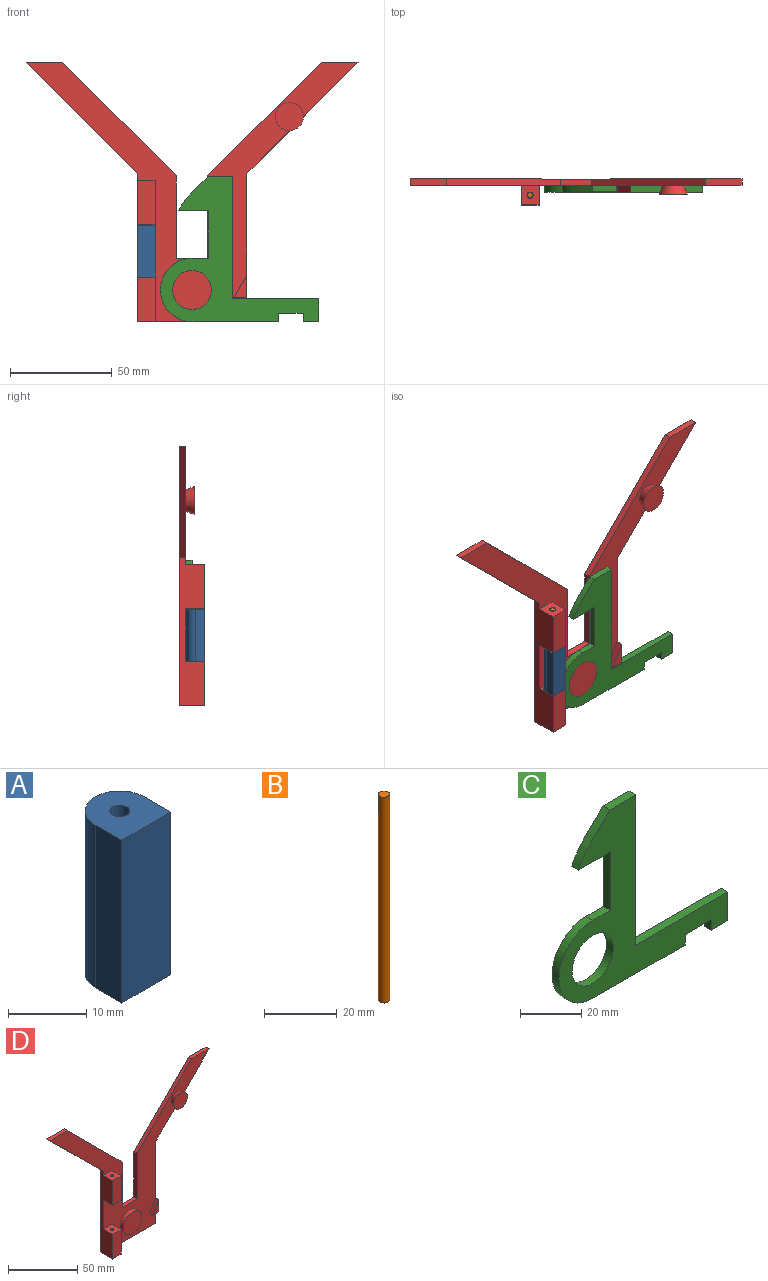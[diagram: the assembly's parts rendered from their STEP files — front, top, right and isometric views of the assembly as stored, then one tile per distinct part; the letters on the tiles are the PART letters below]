
ASSEMBLY  parts=4 mates=3
PART A: 7 faces, bbox 8.8x9.2x25.4 mm
  f0: cylinder r=4.41mm len=25.4mm, axis (0,0,-1), area 352mm2, adj f1,f4,f5,f6
  f1: plane 25.4x4.76mm, normal (-1,0,0), area 121mm2, adj f0,f2,f5,f6
  f2: plane 25.4x8.82mm, normal (0,-1,0), area 224.1mm2, adj f1,f4,f5,f6
  f3: cylinder r=1.27mm len=25.4mm, axis (0,0,-1), area 202.7mm2, adj f5,f6
  f4: plane 25.4x4.76mm, normal (1,0,0), area 121mm2, adj f0,f2,f5,f6
  f5: plane 9.17x8.82mm, normal (0,0,1), area 67.5mm2, adj f0,f1,f2,f3,f4
  f6: plane 9.17x8.82mm, normal (0,0,-1), area 67.5mm2, adj f0,f1,f2,f3,f4
PART B: 3 faces, bbox 3x3x69.3 mm
  f0: cylinder r=1.52mm len=69.34mm, axis (0,0,1), area 664mm2, adj f1,f2
  f1: plane 3.05x3.05mm, normal (0,0,-1), area 7.3mm2, adj f0
  f2: plane 3.05x3.05mm, normal (0,0,1), area 7.3mm2, adj f0
PART C: 17 faces, bbox 77.8x3.2x71.3 mm
  f0: plane 8.14x3.18mm, normal (0,0,1), area 25.8mm2, adj f1,f13,f15,f16
  f1: cylinder r=15.54mm len=31.08mm, axis (0,1,0), area 155mm2, adj f0,f2,f15,f16
  f2: plane 42.57x3.18mm, normal (0,0,-1), area 135.2mm2, adj f1,f3,f15,f16
  f3: plane 4.14x3.18mm, normal (1,0,0), area 13.2mm2, adj f2,f4,f15,f16
  f4: plane 11.94x3.18mm, normal (0,0,-1), area 37.9mm2, adj f3,f5,f15,f16
  f5: plane 4.14x3.18mm, normal (-1,0,0), area 13.2mm2, adj f4,f6,f15,f16
  f6: plane 7.77x3.18mm, normal (0,0,-1), area 24.7mm2, adj f5,f7,f15,f16
  f7: plane 11.28x3.18mm, normal (1,0,0), area 35.8mm2, adj f6,f8,f15,f16
  f8: plane 42.46x3.18mm, normal (0,0,1), area 134.8mm2, adj f7,f9,f15,f16
  f9: plane 59.98x3.18mm, normal (1,0,0), area 190.4mm2, adj f8,f10,f15,f16
  f10: plane 11.83x3.18mm, normal (0,0,1), area 37.6mm2, adj f9,f11,f15,f16
  f11: extruded ~16.81x14.53mm, area 71mm2, adj f10,f12,f15,f16
  f12: plane 14.68x3.18mm, normal (0,0,-1), area 46.6mm2, adj f11,f13,f15,f16
  f13: plane 23.37x3.18mm, normal (-1,0,0), area 74.2mm2, adj f0,f12,f15,f16
  f14: cylinder r=9.53mm len=19.05mm, axis (0,1,0), area 190mm2, adj f15,f16
  f15: plane 77.83x71.26mm, normal (0,-1,0), area 1749.6mm2, adj f0,f1,f2,f3,f4,f5,f6,f7
  f16: plane 77.83x71.26mm, normal (0,1,0), area 1749.6mm2, adj f0,f1,f2,f3,f4,f5,f6,f7
PART D: 30 faces, bbox 162.9x12.7x127.3 mm
  f0: plane 162.92x127.34mm, normal (0,-1,0), area 4448.9mm2, adj f1,f2,f3,f4,f5,f6,f7,f8
  f1: plane 54.52x54.52mm, normal (0.71,0,-0.71), area 242.5mm2, adj f0,f5,f6,f13,f16
  f2: plane 54.52x54.52mm, normal (-0.71,0,-0.71), area 244.8mm2, adj f0,f3,f12,f13
  f3: plane 72.82x12.7mm, normal (-1,0,0), area 644.3mm2, adj f0,f2,f4,f13,f22,f23,f24,f25
  f4: plane 53.88x12.7mm, normal (0,0,-1), area 250mm2, adj f0,f3,f5,f13,f21,f23,f29
  f5: plane 72.82x6.35mm, normal (1,0,0), area 266.6mm2, adj f0,f1,f4,f13,f18,f19,f20
  f6: plane 17.96x3.18mm, normal (0,0,1), area 57mm2, adj f0,f1,f7,f13
  f7: plane 55.84x55.84mm, normal (-0.71,0,0.71), area 250.7mm2, adj f0,f6,f8,f13
  f8: plane 40.44x3.18mm, normal (-1,0,0), area 128.4mm2, adj f0,f7,f9,f13
  f9: plane 15.33x3.18mm, normal (0,0,1), area 48.7mm2, adj f0,f8,f10,f13
  f10: plane 40.44x3.18mm, normal (1,0,0), area 128.4mm2, adj f0,f9,f11,f13
  f11: plane 55.84x55.84mm, normal (0.71,0,0.71), area 250.7mm2, adj f0,f10,f12,f13
  f12: plane 17.96x3.18mm, normal (0,0,1), area 57mm2, adj f0,f2,f11,f13
  f13: plane 162.92x127.34mm, normal (0,1,0), area 5240.1mm2, adj f1,f2,f3,f4,f5,f6,f7,f8
  f14: cylinder r=9.53mm len=19.05mm, axis (0,1,0), area 190mm2, adj f0,f15
  f15: plane 19.05x19.05mm, normal (0,-1,0), area 285mm2, adj f14
  f16: cone r=4.16mm half-angle=20deg, axis (0,-1,0), area 184.4mm2, adj f0,f1,f17
  f17: plane 13.86x13.86mm, normal (0,-1,0), area 150.9mm2, adj f16
  f18: plane 6.42x3.18mm, normal (0,0,-1), area 20.4mm2, adj f0,f5,f19,f20
  f19: plane 11.13x6.42mm, normal (-0.87,0,0.5), area 40.8mm2, adj f0,f5,f18,f20
  f20: plane 11.13x6.42mm, normal (0,-1,0), area 35.8mm2, adj f5,f18,f19
  f21: plane 21.68x9.53mm, normal (1,0,0), area 206.5mm2, adj f0,f4,f22,f23
  f22: plane 9.53x8.82mm, normal (0,0,1), area 79mm2, adj f0,f3,f21,f23,f29
  f23: plane 21.68x8.82mm, normal (0,-1,0), area 191.3mm2, adj f3,f4,f21,f22
  f24: plane 9.53x8.82mm, normal (0,0,1), area 79mm2, adj f0,f3,f26,f27,f28
  f25: plane 9.53x8.82mm, normal (0,0,-1), area 79mm2, adj f0,f3,f26,f27,f28
  f26: plane 21.68x9.53mm, normal (1,0,0), area 206.5mm2, adj f0,f24,f25,f27
  f27: plane 21.68x8.82mm, normal (0,-1,0), area 191.3mm2, adj f3,f24,f25,f26
  f28: cylinder r=1.27mm len=21.68mm, axis (0,0,1), area 173mm2, adj f24,f25
  f29: cylinder r=1.27mm len=21.68mm, axis (0,0,1), area 173mm2, adj f4,f22
PLACE A t=(22.99,-1.37,-24.31)mm fixed
PLACE B t=(63.13,9.26,23.06)mm
PLACE C rot(axis=(0.02,-0.02,1),0deg) t=(22.99,-1.37,23.06)mm
PLACE D t=(22.99,-1.37,23.06)mm
MATE fastened C.f14 <-> D.f14  axis (0,-1,0) through (22.99,-7.72,-30.68)mm
MATE fastened A.f0 <-> B.f0  axis (0,0,-1) through (0.46,-9.31,-11.61)mm
MATE fastened B.f0 <-> D.f28  axis (0,0,1) through (0.46,-9.31,23.06)mm
